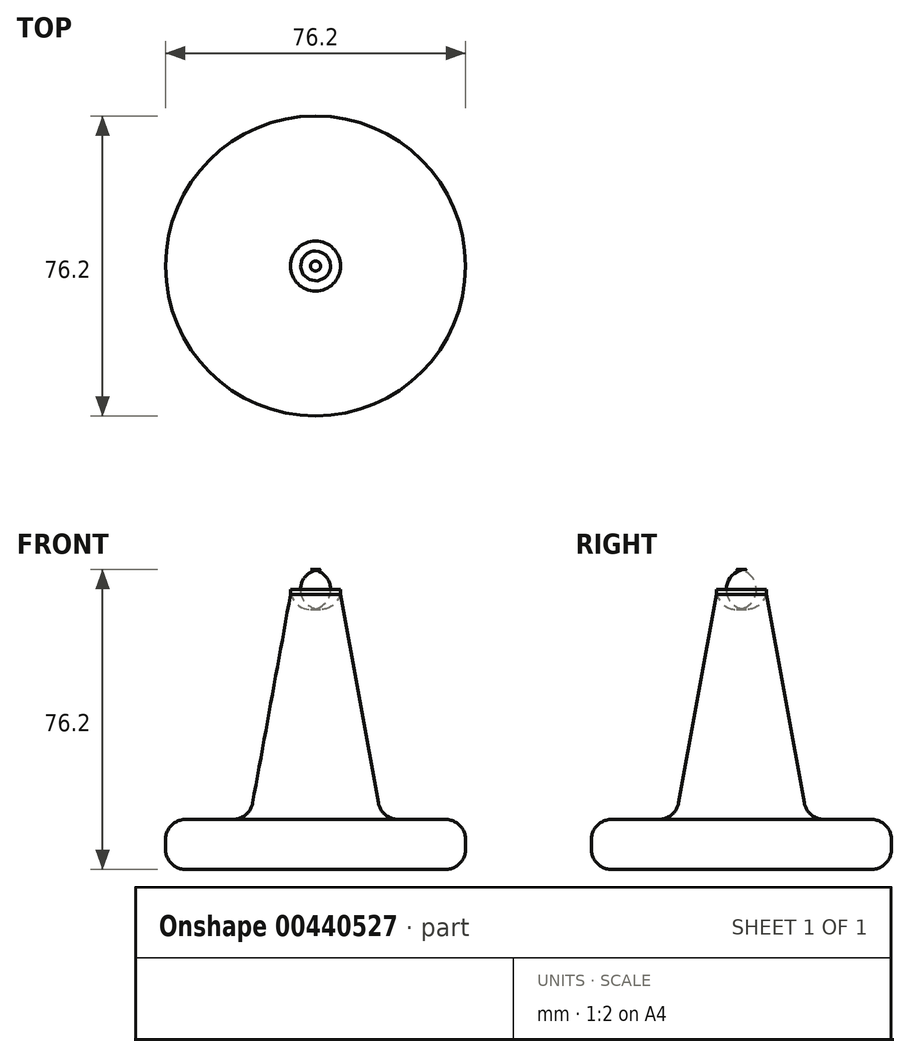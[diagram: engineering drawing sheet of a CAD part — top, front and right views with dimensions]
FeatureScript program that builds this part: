
annotation { "Feature Type Name" : "Feature", "Feature Type Description" : "" }
export const myFeature = defineFeature(function(context is Context, id is Id, definition is map)
    precondition{}
    {
        {
            var Q0;
            Q0=qCreatedBy(makeId("Top.planeOp"),FACE);
            var sketch = newSketch(context, id + "F0", { "sketchPlane" : qUnion([Q0])});
            skCircle(sketch, "E0", {"center": v(0, 0) * mm, "radius": 38.1 * mm});
            skSolve(sketch);
        }
        {
            var Q0;
            Q0 = qSketchRegion(id + "F0", true);
            extrude(context, id + "F1", {"entities" : qUnion([Q0]), "depth" : 12.7 * mm});
        }
        {
            var Q0;
            Q0=qCreatedBy(makeId("Front.planeOp"),FACE);
            var sketch = newSketch(context, id + "F2", { "sketchPlane" : qUnion([Q0])});
            skLineSegment(sketch, "E1", {"start": v(0, 12.7) * mm, "end": v(0, 69.85) * mm});
            skLineSegment(sketch, "E2", {"start": v(6.35, 69.85) * mm, "end": v(16.74, 12.7) * mm});
            skLineSegment(sketch, "E3.top", {"start": v(0, 76.2) * mm, "end": v(6.35, 76.2) * mm});
            skLineSegment(sketch, "E3.left", {"start": v(0, 69.85) * mm, "end": v(0, 76.2) * mm});
            skLineSegment(sketch, "E3.right", {"start": v(6.35, 69.85) * mm, "end": v(6.35, 76.2) * mm});
            skLineSegment(sketch, "E4", {"start": v(0, 12.7) * mm, "end": v(16.74, 12.7) * mm});
            skSolve(sketch);
        }
        {
            var Q0;
            Q0 = qSketchRegion(id + "F2", true);
            var Q1;
            Q1=sQuery(id+"F2.wireOp",EDGE,"E1");
            revolve(context, id + "F3", {"operationType" : NewBodyOperationType.ADD, "entities" : qUnion([Q0]), "axis" : qUnion([Q1]), "revolveType" : RevolveType.FULL});
        }
        {
            var Q0;
            Q0=makeQuery(id+"F1.opExtrude","CAP_EDGE",EDGE,{"disambiguationData":[OSD([sQuery(id+"F0.wireOp",EDGE,"E0")])],"isStart":false});
            var Q1;
            Q1=makeQuery(id+"F1.opExtrude","CAP_EDGE",EDGE,{"disambiguationData":[OSD([sQuery(id+"F0.wireOp",EDGE,"E0")])],"isStart":true});
            var Q2;
            Q2=makeQuery(id+"F3.opRevolve","SWEPT_EDGE",EDGE,{"disambiguationData":[OSD([sQuery(id+"F2.wireOp",EDGE,"E3.top"),sQuery(id+"F2.wireOp",EDGE,"E3.right")])]});
            var Q3;
            Q3=makeQuery(id+"F3.boolean.opBoolean","INTERSECT",EDGE,{"derivedFrom":[makeQuery(id+"F1.opExtrude","CAP_FACE",FACE,{"disambiguationData":[OSD([sQuery(id+"F0.wireOp",EDGE,"E0")])],"isStart":false}),makeQuery(id+"F3.opRevolve","SWEPT_FACE",FACE,{"disambiguationData":[OSD([sQuery(id+"F2.wireOp",EDGE,"E2")])]})]});
            var Q4;
            Q4=makeQuery(id+"F3.opRevolve","SWEPT_EDGE",EDGE,{"disambiguationData":[OSD([sQuery(id+"F2.wireOp",EDGE,"E2"),sQuery(id+"F2.wireOp",EDGE,"E4")])]});
            fillet(context, id + "F4", {"entities" : qUnion([Q0, Q1, Q2, Q3, Q4]), "radius" : 5.08 * mm, "tangentPropagation" : true, "allowEdgeOverflow" : false});
        }
    });
